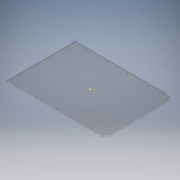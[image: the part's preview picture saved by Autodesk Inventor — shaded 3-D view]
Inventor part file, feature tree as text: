
AUTODESK INVENTOR PART (.ipt)
format: ipt  version: 2019.4 (Build 234330000, 330)  size: 155,648 bytes
history: native  units: mm
features: sketch x5, extrude x3
ambient origin geometry x8: Origin, YZ Plane, XZ Plane, XY Plane, X Axis, Y Axis, Z Axis, Center Point
bodies: Solid1 (feature_tree)
feature tree (8):
  extrude  "Extrusion1"  Depth=337.83mm
  extrude  "Extrusion2"  Depth=20.0mm
  extrude  "Extrusion3"  Depth=5.0mm
  sketch  "Sketch5"  dims[d7=90.0deg]
  sketch  "Sketch6"  dims[d8=15.0mm d9=32.0mm d10=5.0mm d11=0.0mm d14=40.0mm d15=8.732mm d16=5.5mm d17=40.0mm d19=100.0mm d20=10.0mm d22=10.0mm d24=60.0mm d25=8.732mm d26=5.5mm d27=40.0mm d29=100.0mm d30=10.0mm d32=10.0mm d34=10.0mm d35=0.0mm d36=480.0mm d37=339.0mm]
  sketch  "Sketch1"  dims[d0=480.0mm d1=337.83mm]
  sketch  "Sketch2"  dims[d2=5.0mm d3=0.0mm d4=20.0mm]
  sketch  "Sketch4"  dims[d5=12.0mm d6=5.0mm]
